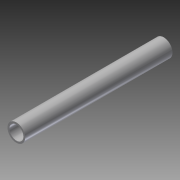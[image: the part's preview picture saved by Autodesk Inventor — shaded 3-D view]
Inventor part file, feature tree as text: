
AUTODESK INVENTOR PART (.ipt)
format: ipt  version: 2013 (Build 170138000, 138)  size: 73,728 bytes
history: native  units: in
note: dims shown in document units (in); Inventor stores cm internally (conversion verified against a paired STEP export)
features: extrude x1, sketch x1
ambient origin geometry x8: Origin, YZ Plane, XZ Plane, XY Plane, X Axis, Y Axis, Z Axis, Center Point
bodies: Solid1 (feature_tree)
feature tree (2):
  extrude  "Extrusion1"  Depth=1.05in
  sketch  "Sketch1"  dims[d0=1.32in d2=1.05in d3=11.0in d4=0.0in]
